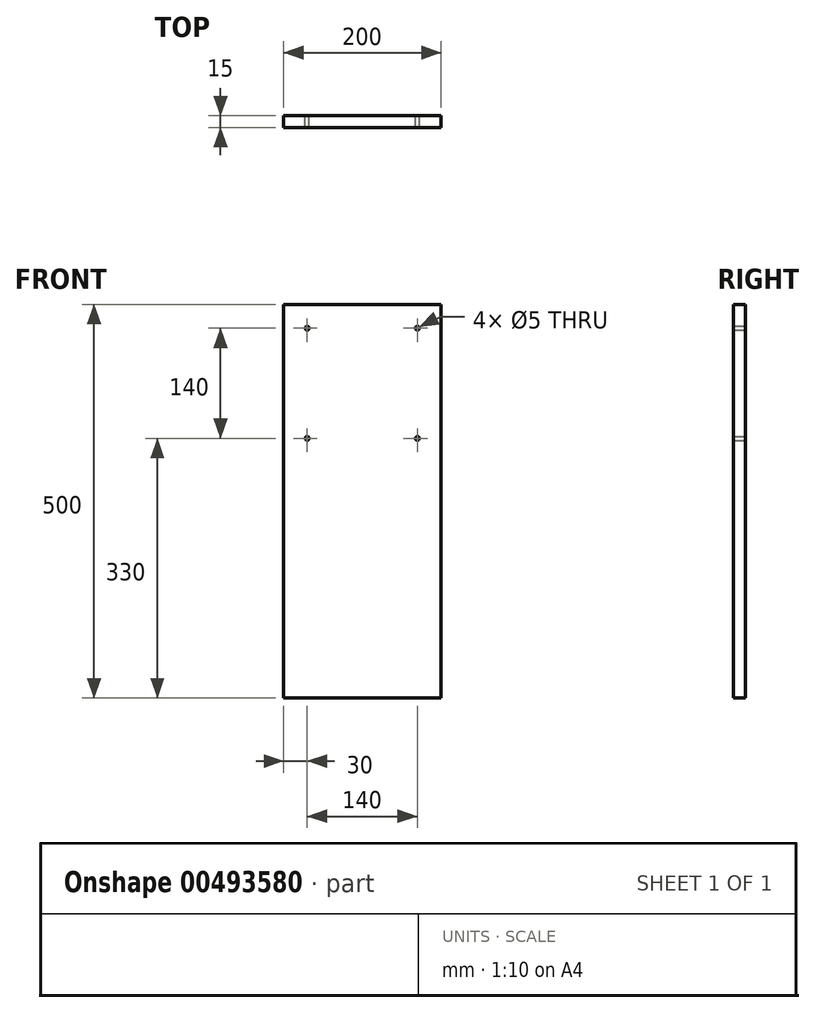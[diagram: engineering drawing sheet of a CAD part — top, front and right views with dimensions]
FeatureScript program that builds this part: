
annotation { "Feature Type Name" : "Feature", "Feature Type Description" : "" }
export const myFeature = defineFeature(function(context is Context, id is Id, definition is map)
    precondition{}
    {
        {
            var Q0;
            Q0=qCreatedBy(makeId("Front.planeOp"),FACE);
            var sketch = newSketch(context, id + "F0", { "sketchPlane" : qUnion([Q0])});
            skLineSegment(sketch, "E0.bottom", {"start": v(0, 0) * mm, "end": v(200, 0) * mm});
            skLineSegment(sketch, "E0.top", {"start": v(0, -500) * mm, "end": v(200, -500) * mm});
            skLineSegment(sketch, "E0.left", {"start": v(0, 0) * mm, "end": v(0, -500) * mm});
            skLineSegment(sketch, "E0.right", {"start": v(200, 0) * mm, "end": v(200, -500) * mm});
            skLineSegment(sketch, "E1.0", {"start": v(0, -30) * mm, "end": v(200, -30) * mm, "construction": true});
            skLineSegment(sketch, "E2.0", {"start": v(170, 0) * mm, "end": v(170, -500) * mm, "construction": true});
            skLineSegment(sketch, "E3.0", {"start": v(30, 0) * mm, "end": v(30, -500) * mm, "construction": true});
            skLineSegment(sketch, "E4.0", {"start": v(0, -170) * mm, "end": v(200, -170) * mm, "construction": true});
            skCircle(sketch, "E5", {"center": v(30, -30) * mm, "radius": 2.5 * mm});
            skCircle(sketch, "E6", {"center": v(170, -30) * mm, "radius": 2.5 * mm});
            skCircle(sketch, "E7", {"center": v(170, -170) * mm, "radius": 2.5 * mm});
            skCircle(sketch, "E8", {"center": v(30, -170) * mm, "radius": 2.5 * mm});
            skSolve(sketch);
        }
        {
            var Q0;
            Q0=makeQuery(id+"F0.imprint","IMPRINT",FACE,{"disambiguationData":[TD([[makeQuery(id+"F0.imprint","IMPRINT",EDGE,{"derivedFrom":sQuery(id+"F0.wireOp",EDGE,"E0.bottom")}),-1.0]])]});
            extrude(context, id + "F1", {"entities" : qUnion([Q0]), "endBound" : BoundingType.SYMMETRIC, "depth" : 15 * mm});
        }
    });
